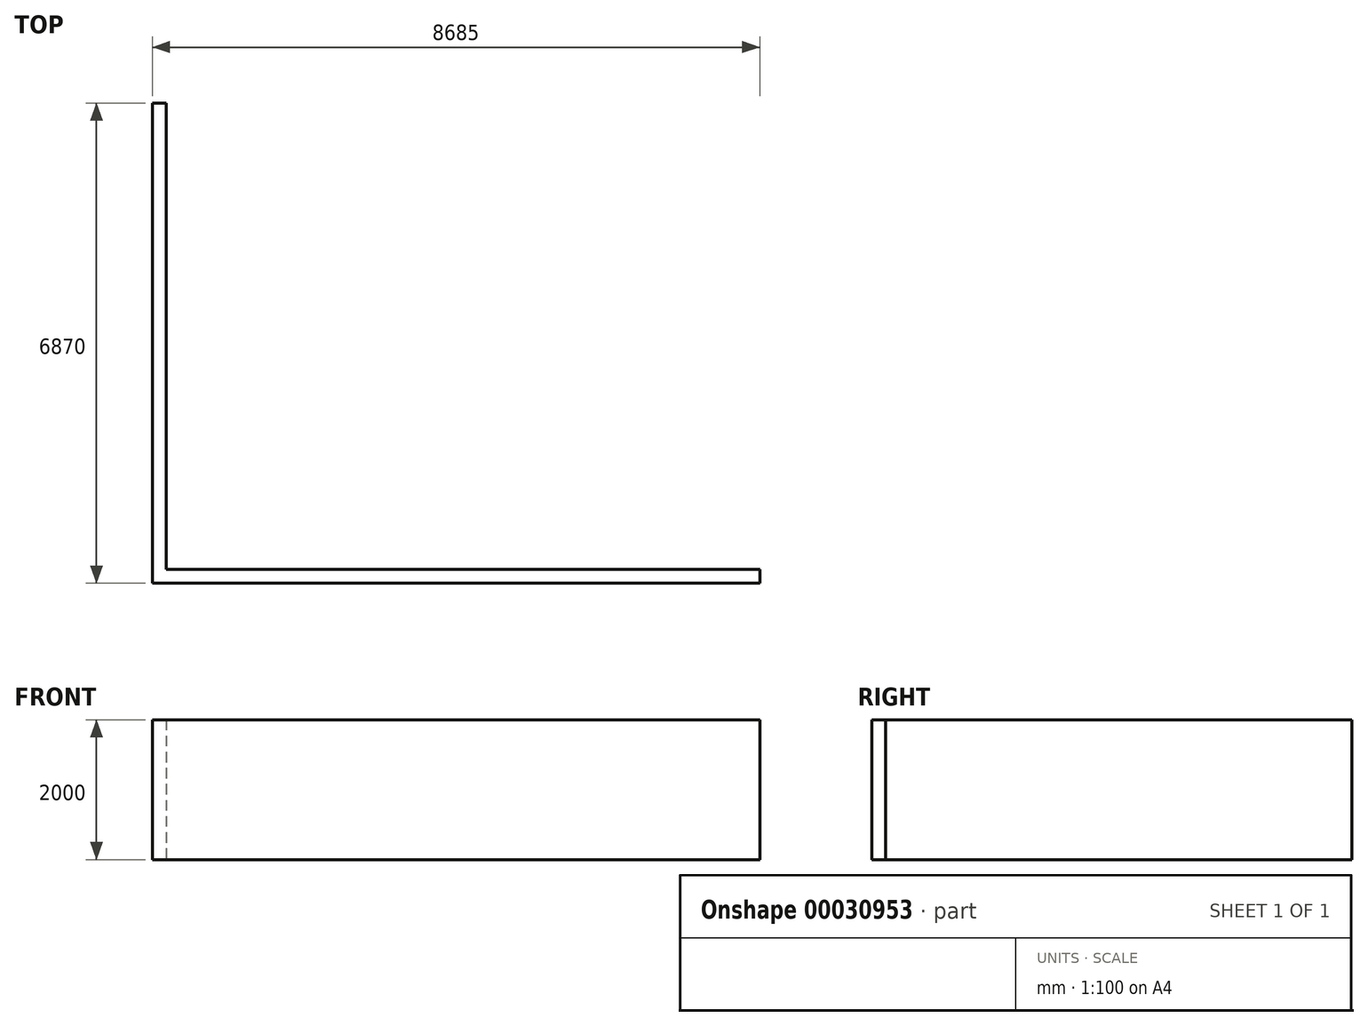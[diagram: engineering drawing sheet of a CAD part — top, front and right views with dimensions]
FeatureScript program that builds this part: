
annotation { "Feature Type Name" : "Feature", "Feature Type Description" : "" }
export const myFeature = defineFeature(function(context is Context, id is Id, definition is map)
    precondition{}
    {
        {
            var Q0;
            Q0=qCreatedBy(makeId("Top.planeOp"),FACE);
            var sketch = newSketch(context, id + "F0", { "sketchPlane" : qUnion([Q0])});
            skLineSegment(sketch, "E0", {"start": v(0, 0) * mm, "end": v(0, 6670) * mm});
            skLineSegment(sketch, "E1", {"start": v(0, 6670) * mm, "end": v(-200, 6670) * mm});
            skLineSegment(sketch, "E2", {"start": v(-200, 6670) * mm, "end": v(-200, -200) * mm});
            skLineSegment(sketch, "E3", {"start": v(-200, -200) * mm, "end": v(8485, -200) * mm});
            skLineSegment(sketch, "E4", {"start": v(8485, -200) * mm, "end": v(8485, 0) * mm});
            skLineSegment(sketch, "E5", {"start": v(8485, 0) * mm, "end": v(0, 0) * mm});
            skSolve(sketch);
        }
        {
            var Q0;
            Q0=makeQuery(id+"F0.imprint","IMPRINT",FACE,{"disambiguationData":[TD([[makeQuery(id+"F0.imprint","IMPRINT",EDGE,{"derivedFrom":sQuery(id+"F0.wireOp",EDGE,"E0")}),1.0]])]});
            extrude(context, id + "F1", {"entities" : qUnion([Q0]), "depth" : 2000 * mm});
        }
    });
